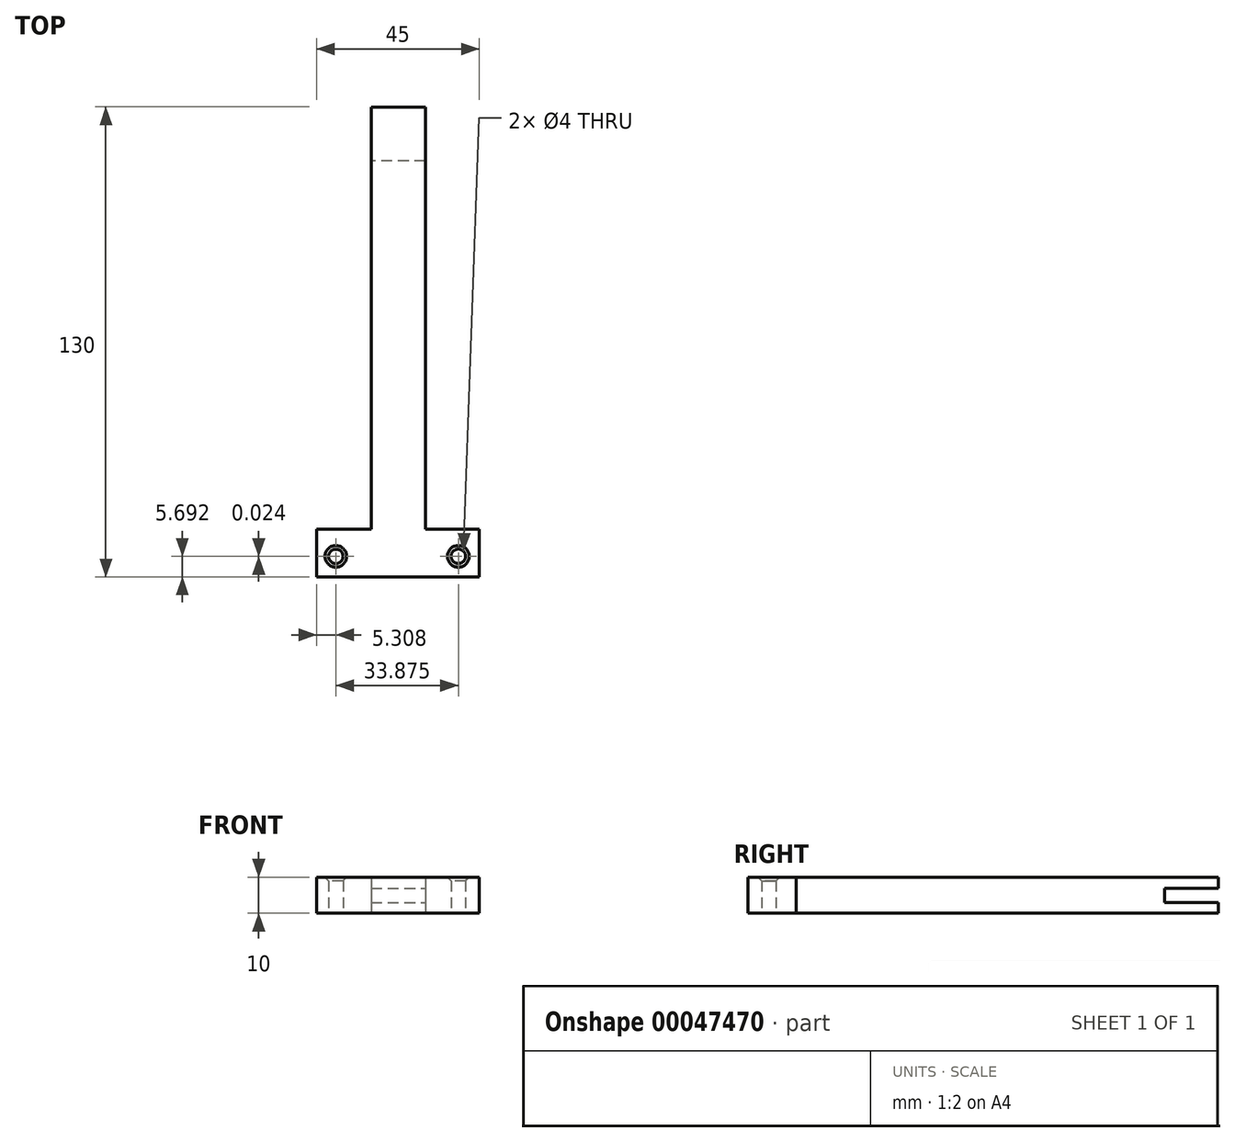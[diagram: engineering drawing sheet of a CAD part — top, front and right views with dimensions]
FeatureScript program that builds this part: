
annotation { "Feature Type Name" : "Feature", "Feature Type Description" : "" }
export const myFeature = defineFeature(function(context is Context, id is Id, definition is map)
    precondition{}
    {
        {
            var Q0;
            Q0=qCreatedBy(makeId("Top.planeOp"),FACE);
            var sketch = newSketch(context, id + "F0", { "sketchPlane" : qUnion([Q0])});
            skLineSegment(sketch, "E0.bottom", {"start": v(-15, 79.56) * mm, "end": v(0, 79.56) * mm});
            skLineSegment(sketch, "E0.top", {"start": v(-15, -50.44) * mm, "end": v(0, -50.44) * mm});
            skLineSegment(sketch, "E0.left", {"start": v(-15, 79.56) * mm, "end": v(-15, -50.44) * mm});
            skLineSegment(sketch, "E0.right", {"start": v(0, 79.56) * mm, "end": v(0, -50.44) * mm});
            skLineSegment(sketch, "E1.bottom", {"start": v(-30.08, -37.2) * mm, "end": v(14.92, -37.2) * mm});
            skLineSegment(sketch, "E1.top", {"start": v(-30.08, -50.44) * mm, "end": v(14.92, -50.44) * mm});
            skLineSegment(sketch, "E1.left", {"start": v(-30.08, -37.2) * mm, "end": v(-30.08, -50.44) * mm});
            skLineSegment(sketch, "E1.right", {"start": v(14.92, -37.2) * mm, "end": v(14.92, -50.44) * mm});
            skSolve(sketch);
        }
        {
            var Q0;
            Q0 = qSketchRegion(id + "F0", true);
            extrude(context, id + "F1", {"entities" : qUnion([Q0]), "depth" : 10 * mm});
        }
        {
            var Q0;
            Q0=qCreatedBy(makeId("Top.planeOp"),FACE);
            var sketch = newSketch(context, id + "F2", { "sketchPlane" : qUnion([Q0])});
            skCircle(sketch, "E2", {"center": v(9.1, -44.72) * mm, "radius": 2 * mm});
            skCircle(sketch, "E3", {"center": v(-24.77, -44.75) * mm, "radius": 2 * mm});
            skSolve(sketch);
        }
        {
            var Q0;
            Q0 = qSketchRegion(id + "F2", true);
            extrude(context, id + "F3", {"entities" : qUnion([Q0]), "operationType" : NewBodyOperationType.REMOVE, "endBound" : BoundingType.THROUGH_ALL, "depth" : 25 * mm});
        }
        {
            var Q0;
            Q0=makeQuery(id+"F3.boolean.opBoolean","INTERSECT",EDGE,{"derivedFrom":[makeQuery(id+"F1.opExtrude","CAP_FACE",FACE,{"disambiguationData":[OSD([sQuery(id+"F0.wireOp",EDGE,"E0.bottom"),sQuery(id+"F0.wireOp",EDGE,"E0.left"),sQuery(id+"F0.wireOp",EDGE,"E0.right"),sQuery(id+"F0.wireOp",EDGE,"E1.bottom"),sQuery(id+"F0.wireOp",EDGE,"E1.top"),sQuery(id+"F0.wireOp",EDGE,"E1.left"),sQuery(id+"F0.wireOp",EDGE,"E1.right")])],"isStart":false}),makeQuery(id+"F3.opExtrude","SWEPT_FACE",FACE,{"disambiguationData":[OSD([sQuery(id+"F2.wireOp",EDGE,"E3")])]})]});
            var Q1;
            Q1=makeQuery(id+"F3.boolean.opBoolean","INTERSECT",EDGE,{"derivedFrom":[makeQuery(id+"F1.opExtrude","CAP_FACE",FACE,{"disambiguationData":[OSD([sQuery(id+"F0.wireOp",EDGE,"E0.bottom"),sQuery(id+"F0.wireOp",EDGE,"E0.left"),sQuery(id+"F0.wireOp",EDGE,"E0.right"),sQuery(id+"F0.wireOp",EDGE,"E1.bottom"),sQuery(id+"F0.wireOp",EDGE,"E1.top"),sQuery(id+"F0.wireOp",EDGE,"E1.left"),sQuery(id+"F0.wireOp",EDGE,"E1.right")])],"isStart":false}),makeQuery(id+"F3.opExtrude","SWEPT_FACE",FACE,{"disambiguationData":[OSD([sQuery(id+"F2.wireOp",EDGE,"E2")])]})]});
            chamfer(context, id + "F4", {"entities" : qUnion([Q0, Q1]), "width" : 1 * mm, "tangentPropagation" : true});
        }
        {
            var Q0;
            Q0=qCreatedBy(makeId("Front.planeOp"),FACE);
            var sketch = newSketch(context, id + "F5", { "sketchPlane" : qUnion([Q0])});
            skLineSegment(sketch, "E4.bottom", {"start": v(0, 6.94) * mm, "end": v(-15.3, 6.94) * mm});
            skLineSegment(sketch, "E4.top", {"start": v(0, 2.94) * mm, "end": v(-15.3, 2.94) * mm});
            skLineSegment(sketch, "E4.left", {"start": v(0, 6.94) * mm, "end": v(0, 2.94) * mm});
            skLineSegment(sketch, "E4.right", {"start": v(-15.3, 6.94) * mm, "end": v(-15.3, 2.94) * mm});
            skSolve(sketch);
        }
        {
            var Q0;
            Q0=makeQuery(id+"F1.opExtrude","SWEPT_FACE",FACE,{"disambiguationData":[OSD([sQuery(id+"F0.wireOp",EDGE,"E0.bottom")])]});
            var Q1;
            Q1=makeQuery(id+"F5.imprint","IMPRINT",FACE,{"disambiguationData":[TD([[makeQuery(id+"F5.imprint","IMPRINT",EDGE,{"derivedFrom":sQuery(id+"F5.wireOp",EDGE,"E4.bottom")}),1.0]])]});
            var Q2;
            Q2=sQuery(id+"F5.wireOp",EDGE,"E4.left");
            extrude(context, id + "F6", {"entities" : qUnion([Q0, Q1]), "operationType" : NewBodyOperationType.REMOVE, "surfaceEntities" : qUnion([Q2]), "endBound" : BoundingType.THROUGH_ALL, "depth" : 25 * mm, "hasSecondDirection" : true, "secondDirectionOppositeDirection" : false, "secondDirectionDepth" : 64.63 * mm});
        }
    });
